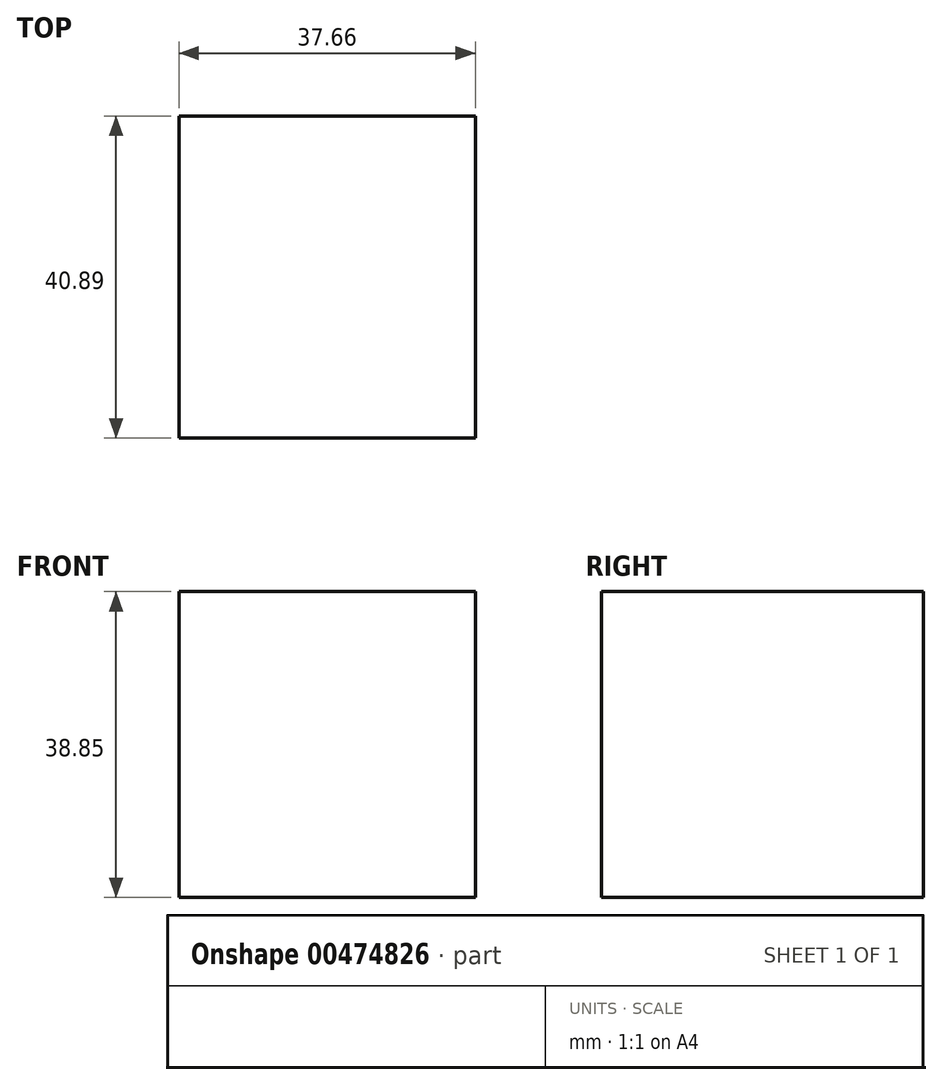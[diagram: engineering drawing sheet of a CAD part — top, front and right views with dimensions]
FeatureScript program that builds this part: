
annotation { "Feature Type Name" : "Feature", "Feature Type Description" : "" }
export const myFeature = defineFeature(function(context is Context, id is Id, definition is map)
    precondition{}
    {
        {
            var Q0;
            Q0=qCreatedBy(makeId("Front.planeOp"),FACE);
            var sketch = newSketch(context, id + "F0", { "sketchPlane" : qUnion([Q0])});
            skLineSegment(sketch, "E0.bottom", {"start": v(0, 0) * mm, "end": v(37.66, 0) * mm});
            skLineSegment(sketch, "E0.top", {"start": v(0, 38.85) * mm, "end": v(37.66, 38.85) * mm});
            skLineSegment(sketch, "E0.left", {"start": v(0, 0) * mm, "end": v(0, 38.85) * mm});
            skLineSegment(sketch, "E0.right", {"start": v(37.66, 0) * mm, "end": v(37.66, 38.85) * mm});
            skSolve(sketch);
        }
        {
            var Q0;
            Q0=makeQuery(id+"F0.imprint","IMPRINT",FACE,{"disambiguationData":[TD([[makeQuery(id+"F0.imprint","IMPRINT",EDGE,{"derivedFrom":sQuery(id+"F0.wireOp",EDGE,"E0.bottom")}),1.0]])]});
            extrude(context, id + "F1", {"entities" : qUnion([Q0]), "depth" : 40.9 * mm});
        }
    });
